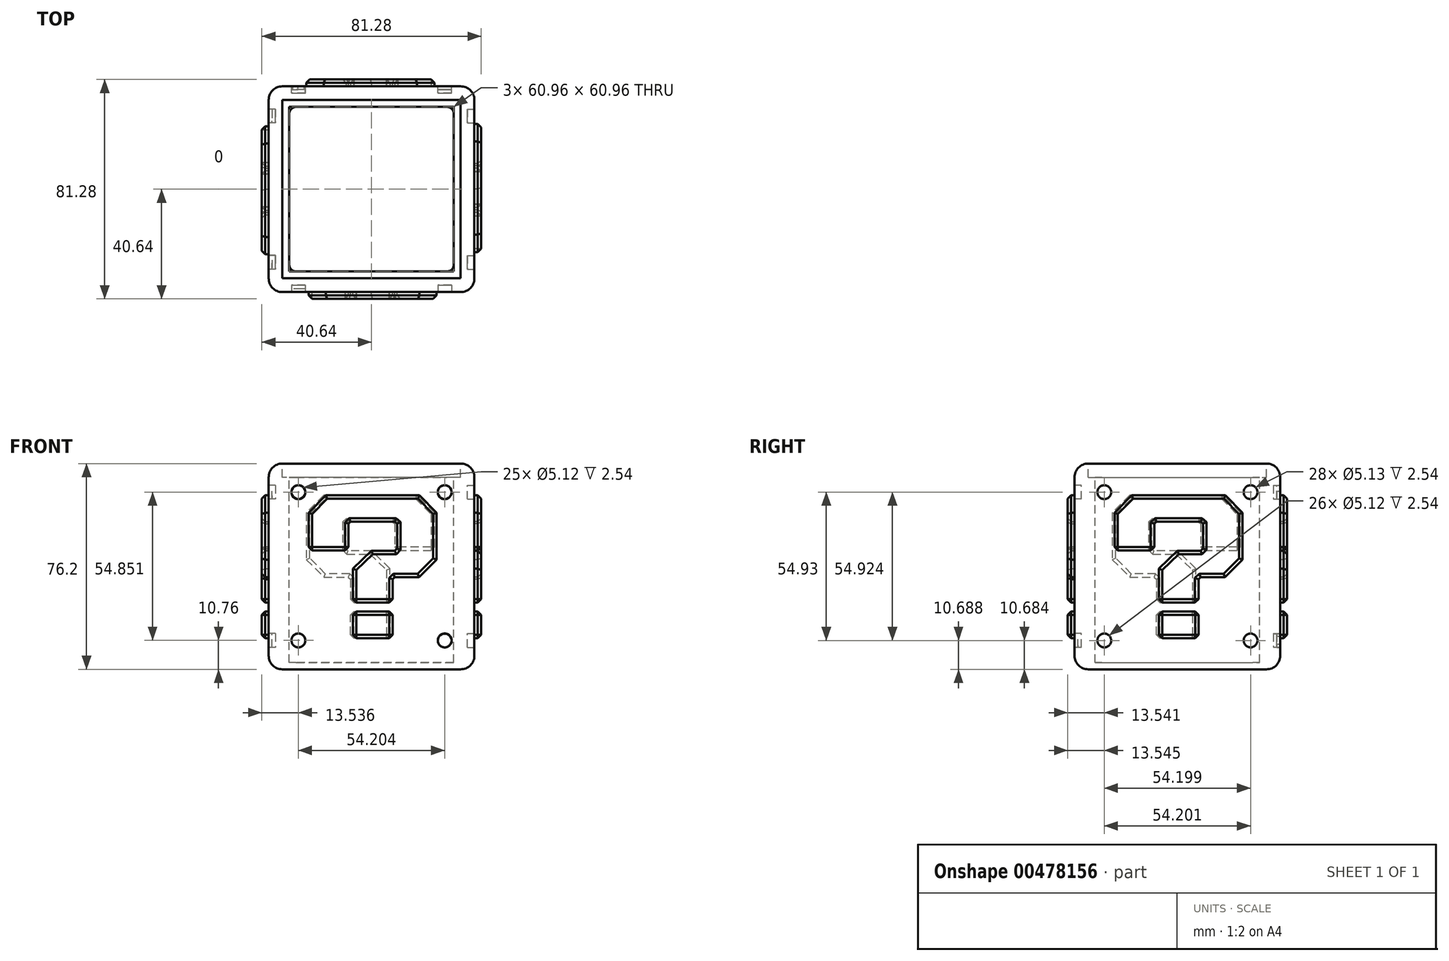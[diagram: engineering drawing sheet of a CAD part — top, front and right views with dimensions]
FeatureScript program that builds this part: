
annotation { "Feature Type Name" : "Feature", "Feature Type Description" : "" }
export const myFeature = defineFeature(function(context is Context, id is Id, definition is map)
    precondition{}
    {
        {
            var Q0;
            Q0=qCreatedBy(makeId("Top.planeOp"),FACE);
            var sketch = newSketch(context, id + "F0", { "sketchPlane" : qUnion([Q0])});
            skLineSegment(sketch, "E0.bottom", {"start": v(38.1, 38.1) * mm, "end": v(-38.1, 38.1) * mm});
            skLineSegment(sketch, "E0.top", {"start": v(38.1, -38.1) * mm, "end": v(-38.1, -38.1) * mm});
            skLineSegment(sketch, "E0.left", {"start": v(38.1, 38.1) * mm, "end": v(38.1, -38.1) * mm});
            skLineSegment(sketch, "E0.right", {"start": v(-38.1, 38.1) * mm, "end": v(-38.1, -38.1) * mm});
            skPoint(sketch, "E0.middle", {"position": v(0, 0) * mm});
            skSolve(sketch);
        }
        {
            var Q0;
            Q0=makeQuery(id+"F0.imprint","IMPRINT",FACE,{"disambiguationData":[TD([[makeQuery(id+"F0.imprint","IMPRINT",EDGE,{"derivedFrom":sQuery(id+"F0.wireOp",EDGE,"E0.bottom")}),1.0]])]});
            extrude(context, id + "F1", {"entities" : qUnion([Q0]), "depth" : 76.2 * mm, "offsetDistance" : 25.4 * mm});
        }
        {
            var Q0;
            Q0=makeQuery(id+"F1.opExtrude","CAP_FACE",FACE,{"disambiguationData":[OSD([sQuery(id+"F0.wireOp",EDGE,"E0.bottom"),sQuery(id+"F0.wireOp",EDGE,"E0.top"),sQuery(id+"F0.wireOp",EDGE,"E0.left"),sQuery(id+"F0.wireOp",EDGE,"E0.right")])],"isStart":true});
            var Q1;
            Q1=makeQuery(id+"F1.opExtrude","SWEPT_FACE",FACE,{"disambiguationData":[OSD([sQuery(id+"F0.wireOp",EDGE,"E0.bottom")])]});
            var Q2;
            Q2=makeQuery(id+"F1.opExtrude","SWEPT_FACE",FACE,{"disambiguationData":[OSD([sQuery(id+"F0.wireOp",EDGE,"E0.right")])]});
            var Q3;
            Q3=makeQuery(id+"F1.opExtrude","SWEPT_FACE",FACE,{"disambiguationData":[OSD([sQuery(id+"F0.wireOp",EDGE,"E0.left")])]});
            var Q4;
            Q4=makeQuery(id+"F1.opExtrude","SWEPT_FACE",FACE,{"disambiguationData":[OSD([sQuery(id+"F0.wireOp",EDGE,"E0.top")])]});
            var Q5;
            Q5=makeQuery(id+"F1.opExtrude","CAP_FACE",FACE,{"disambiguationData":[OSD([sQuery(id+"F0.wireOp",EDGE,"E0.bottom"),sQuery(id+"F0.wireOp",EDGE,"E0.top"),sQuery(id+"F0.wireOp",EDGE,"E0.left"),sQuery(id+"F0.wireOp",EDGE,"E0.right")])],"isStart":false});
            fillet(context, id + "F2", {"entities" : qUnion([Q0, Q1, Q2, Q3, Q4, Q5]), "radius" : 5.08 * mm, "tangentPropagation" : true, "allowEdgeOverflow" : false});
        }
        {
            var Q0;
            Q0=makeQuery(id+"F1.opExtrude","SWEPT_FACE",FACE,{"disambiguationData":[OSD([sQuery(id+"F0.wireOp",EDGE,"E0.left")])]});
            var sketch = newSketch(context, id + "F3", { "sketchPlane" : qUnion([Q0])});
            skLineSegment(sketch, "E1", {"start": v(0, 71.12) * mm, "end": v(0, 64.52) * mm});
            skPoint(sketch, "E1.endSnap0", {"position": v(0, 71.12) * mm});
            skLineSegment(sketch, "E2", {"start": v(0, 5.08) * mm, "end": v(0, 11.68) * mm});
            skPoint(sketch, "E2.endSnap0", {"position": v(0, 5.08) * mm});
            skSolve(sketch);
        }
        {
            var Q0;
            {var subQ0=sQuery(id+"F0.wireOp",EDGE,"E0.left");var subQ1=makeQuery(id+"F1.opExtrude","SWEPT_FACE",FACE,{"disambiguationData":[OSD([subQ0])]});var subQ5=makeQuery(id+"F2.opFillet","BLEND_EDGE",EDGE,{"blendedFrom":[makeQuery(id+"F1.opExtrude","SWEPT_EDGE",EDGE,{"disambiguationData":[OSD([sQuery(id+"F0.wireOp",EDGE,"E0.bottom"),subQ0])]}),subQ1],"blendedInto":[subQ1]});Q0=makeQuery(id+"F3.imprint","IMPRINT",FACE,{"disambiguationData":[TD([[makeQuery(id+"F3.imprint","IMPRINT",EDGE,{"derivedFrom":subQ5}),1.0]])]});}
            var sketch = newSketch(context, id + "F4", { "sketchPlane" : qUnion([Q0])});
            skLineSegment(sketch, "E3", {"start": v(-23.33, 57.98) * mm, "end": v(-16.9, 64.41) * mm});
            skLineSegment(sketch, "E4", {"start": v(-16.9, 64.41) * mm, "end": v(17.73, 64.41) * mm});
            skLineSegment(sketch, "E5", {"start": v(17.73, 64.41) * mm, "end": v(24.13, 58) * mm});
            skLineSegment(sketch, "E6", {"start": v(24.13, 58) * mm, "end": v(24.13, 40.64) * mm});
            skLineSegment(sketch, "E7", {"start": v(24.13, 40.64) * mm, "end": v(17.66, 34.17) * mm});
            skLineSegment(sketch, "E8", {"start": v(17.66, 34.17) * mm, "end": v(8.64, 34.17) * mm});
            skLineSegment(sketch, "E9", {"start": v(8.64, 34.17) * mm, "end": v(7.78, 33.32) * mm});
            skLineSegment(sketch, "E10", {"start": v(7.78, 33.32) * mm, "end": v(7.78, 24.73) * mm});
            skLineSegment(sketch, "E11", {"start": v(7.78, 24.73) * mm, "end": v(-6.86, 24.73) * mm});
            skLineSegment(sketch, "E12", {"start": v(-6.86, 24.73) * mm, "end": v(-6.86, 37.33) * mm});
            skLineSegment(sketch, "E13", {"start": v(-6.86, 37.33) * mm, "end": v(0, 43.94) * mm});
            skLineSegment(sketch, "E14", {"start": v(0, 43.94) * mm, "end": v(8.64, 43.94) * mm});
            skLineSegment(sketch, "E15", {"start": v(8.64, 43.94) * mm, "end": v(9.46, 44.76) * mm});
            skLineSegment(sketch, "E16", {"start": v(9.46, 44.76) * mm, "end": v(9.46, 53.96) * mm});
            skLineSegment(sketch, "E17", {"start": v(9.46, 53.96) * mm, "end": v(8.64, 54.74) * mm});
            skLineSegment(sketch, "E18", {"start": v(8.64, 54.74) * mm, "end": v(-7.76, 54.74) * mm});
            skLineSegment(sketch, "E19", {"start": v(-7.76, 54.74) * mm, "end": v(-8.6, 53.9) * mm});
            skLineSegment(sketch, "E20", {"start": v(-8.6, 53.9) * mm, "end": v(-8.6, 44.03) * mm});
            skLineSegment(sketch, "E21", {"start": v(-8.6, 44.03) * mm, "end": v(-23.33, 44.03) * mm});
            skLineSegment(sketch, "E22", {"start": v(-23.33, 44.03) * mm, "end": v(-23.33, 57.98) * mm});
            skLineSegment(sketch, "E23", {"start": v(-6.85, 21.4) * mm, "end": v(-6.85, 11.58) * mm});
            skLineSegment(sketch, "E24", {"start": v(-6.85, 11.58) * mm, "end": v(7.8, 11.58) * mm});
            skLineSegment(sketch, "E25", {"start": v(7.8, 11.58) * mm, "end": v(7.8, 21.4) * mm});
            skLineSegment(sketch, "E26", {"start": v(7.8, 21.4) * mm, "end": v(-6.85, 21.4) * mm});
            skPoint(sketch, "E27.start.orphan", {"position": v(-23.33, 51) * mm});
            skSolve(sketch);
        }
        {
            var Q0;
            {var subQ0=sQuery(id+"F0.wireOp",EDGE,"E0.left");var subQ1=makeQuery(id+"F1.opExtrude","SWEPT_FACE",FACE,{"disambiguationData":[OSD([subQ0])]});var subQ5=makeQuery(id+"F2.opFillet","BLEND_EDGE",EDGE,{"blendedFrom":[makeQuery(id+"F1.opExtrude","SWEPT_EDGE",EDGE,{"disambiguationData":[OSD([sQuery(id+"F0.wireOp",EDGE,"E0.bottom"),subQ0])]}),subQ1],"blendedInto":[subQ1]});Q0=makeQuery(id+"F3.imprint","IMPRINT",FACE,{"disambiguationData":[TD([[makeQuery(id+"F3.imprint","IMPRINT",EDGE,{"derivedFrom":subQ5}),1.0]])]});}
            var sketch = newSketch(context, id + "F5", { "sketchPlane" : qUnion([Q0])});
            skCircle(sketch, "E28", {"center": v(-27.1, 10.68) * mm, "radius": 2.56 * mm});
            skPoint(sketch, "E28.first.point", {"position": v(-29.65, 10.95) * mm});
            skPoint(sketch, "E28.second.point", {"position": v(-24.55, 10.4) * mm});
            skPoint(sketch, "E28.third.point", {"position": v(-26.75, 8.14) * mm});
            skCircle(sketch, "E29.MirrorC", {"center": v(-27.1, 65.6) * mm, "radius": 2.56 * mm});
            skCircle(sketch, "E30.MirrorC", {"center": v(27.1, 65.6) * mm, "radius": 2.56 * mm});
            skCircle(sketch, "E31.MirrorC", {"center": v(27.1, 10.68) * mm, "radius": 2.56 * mm});
            skSolve(sketch);
        }
        {
            var Q0;
            Q0 = qSketchRegion(id + "F4", true);
            extrude(context, id + "F6", {"entities" : qUnion([Q0]), "operationType" : NewBodyOperationType.ADD, "depth" : 2.54 * mm, "offsetDistance" : 25.4 * mm});
        }
        {
            var Q0;
            Q0=makeQuery(id+"F6.opExtrude","CAP_EDGE",EDGE,{"disambiguationData":[OSD([sQuery(id+"F4.wireOp",EDGE,"E4")])],"isStart":false});
            var Q1;
            Q1=makeQuery(id+"F6.opExtrude","CAP_EDGE",EDGE,{"disambiguationData":[OSD([sQuery(id+"F4.wireOp",EDGE,"E3")])],"isStart":false});
            var Q2;
            Q2=makeQuery(id+"F6.opExtrude","CAP_EDGE",EDGE,{"disambiguationData":[OSD([sQuery(id+"F4.wireOp",EDGE,"E22")])],"isStart":false});
            var Q3;
            Q3=makeQuery(id+"F6.opExtrude","CAP_EDGE",EDGE,{"disambiguationData":[OSD([sQuery(id+"F4.wireOp",EDGE,"E21")])],"isStart":false});
            var Q4;
            Q4=makeQuery(id+"F6.opExtrude","CAP_EDGE",EDGE,{"disambiguationData":[OSD([sQuery(id+"F4.wireOp",EDGE,"E20")])],"isStart":false});
            var Q5;
            Q5=makeQuery(id+"F6.opExtrude","CAP_EDGE",EDGE,{"disambiguationData":[OSD([sQuery(id+"F4.wireOp",EDGE,"E19")])],"isStart":false});
            var Q6;
            Q6=makeQuery(id+"F6.opExtrude","CAP_EDGE",EDGE,{"disambiguationData":[OSD([sQuery(id+"F4.wireOp",EDGE,"E18")])],"isStart":false});
            var Q7;
            Q7=makeQuery(id+"F6.opExtrude","CAP_FACE",FACE,{"disambiguationData":[OSD([sQuery(id+"F4.wireOp",EDGE,"E3"),sQuery(id+"F4.wireOp",EDGE,"E4"),sQuery(id+"F4.wireOp",EDGE,"E5"),sQuery(id+"F4.wireOp",EDGE,"E6"),sQuery(id+"F4.wireOp",EDGE,"E7"),sQuery(id+"F4.wireOp",EDGE,"E8"),sQuery(id+"F4.wireOp",EDGE,"E9"),sQuery(id+"F4.wireOp",EDGE,"E10"),sQuery(id+"F4.wireOp",EDGE,"E11"),sQuery(id+"F4.wireOp",EDGE,"E12"),sQuery(id+"F4.wireOp",EDGE,"E13"),sQuery(id+"F4.wireOp",EDGE,"E14"),sQuery(id+"F4.wireOp",EDGE,"E15"),sQuery(id+"F4.wireOp",EDGE,"E16"),sQuery(id+"F4.wireOp",EDGE,"E17"),sQuery(id+"F4.wireOp",EDGE,"E18"),sQuery(id+"F4.wireOp",EDGE,"E19"),sQuery(id+"F4.wireOp",EDGE,"E20"),sQuery(id+"F4.wireOp",EDGE,"E21"),sQuery(id+"F4.wireOp",EDGE,"E22")])],"isStart":false});
            var Q8;
            Q8=makeQuery(id+"F6.opExtrude","CAP_FACE",FACE,{"disambiguationData":[OSD([sQuery(id+"F4.wireOp",EDGE,"E23"),sQuery(id+"F4.wireOp",EDGE,"E24"),sQuery(id+"F4.wireOp",EDGE,"E25"),sQuery(id+"F4.wireOp",EDGE,"E26")])],"isStart":false});
            var Q9;
            Q9=makeQuery(id+"F6.opExtrude","SWEPT_EDGE",EDGE,{"disambiguationData":[OSD([sQuery(id+"F4.wireOp",EDGE,"E23"),sQuery(id+"F4.wireOp",EDGE,"E24")])]});
            var Q10;
            Q10=makeQuery(id+"F6.opExtrude","SWEPT_EDGE",EDGE,{"disambiguationData":[OSD([sQuery(id+"F4.wireOp",EDGE,"E21"),sQuery(id+"F4.wireOp",EDGE,"E22")])]});
            var Q11;
            Q11=makeQuery(id+"F6.opExtrude","SWEPT_EDGE",EDGE,{"disambiguationData":[OSD([sQuery(id+"F4.wireOp",EDGE,"E20"),sQuery(id+"F4.wireOp",EDGE,"E21")])]});
            var Q12;
            Q12=makeQuery(id+"F6.opExtrude","SWEPT_EDGE",EDGE,{"disambiguationData":[OSD([sQuery(id+"F4.wireOp",EDGE,"E10"),sQuery(id+"F4.wireOp",EDGE,"E11")])]});
            var Q13;
            Q13=makeQuery(id+"F6.opExtrude","SWEPT_EDGE",EDGE,{"disambiguationData":[OSD([sQuery(id+"F4.wireOp",EDGE,"E11"),sQuery(id+"F4.wireOp",EDGE,"E12")])]});
            var Q14;
            Q14=makeQuery(id+"F6.opExtrude","SWEPT_EDGE",EDGE,{"disambiguationData":[OSD([sQuery(id+"F4.wireOp",EDGE,"E25"),sQuery(id+"F4.wireOp",EDGE,"E26")])]});
            var Q15;
            Q15=makeQuery(id+"F6.opExtrude","SWEPT_EDGE",EDGE,{"disambiguationData":[OSD([sQuery(id+"F4.wireOp",EDGE,"E24"),sQuery(id+"F4.wireOp",EDGE,"E25")])]});
            var Q16;
            Q16=makeQuery(id+"F6.opExtrude","SWEPT_EDGE",EDGE,{"disambiguationData":[OSD([sQuery(id+"F4.wireOp",EDGE,"E23"),sQuery(id+"F4.wireOp",EDGE,"E26")])]});
            chamfer(context, id + "F7", {"entities" : qUnion([Q0, Q1, Q2, Q3, Q4, Q5, Q6, Q7, Q8, Q9, Q10, Q11, Q12, Q13, Q14, Q15, Q16]), "width" : 1.27 * mm, "tangentPropagation" : true});
        }
        {
            var Q0;
            Q0=qCreatedBy(makeId("Right.planeOp"),FACE);
            var sketch = newSketch(context, id + "F8", { "sketchPlane" : qUnion([Q0])});
            skLineSegment(sketch, "E32", {"start": v(0, 0) * mm, "end": v(0, 88.63) * mm});
            skSolve(sketch);
        }
        {
            var Q0;
            Q0=makeQuery(id+"F1.opExtrude","SWEPT_BODY",BODY,{"disambiguationData":[OSD([sQuery(id+"F0.wireOp",EDGE,"E0.bottom"),sQuery(id+"F0.wireOp",EDGE,"E0.top"),sQuery(id+"F0.wireOp",EDGE,"E0.left"),sQuery(id+"F0.wireOp",EDGE,"E0.right")])]});
            var Q1;
            Q1=sQuery(id+"F8.wireOp",EDGE,"E32");
            transform(context, id + "F9", {"entities" : qUnion([Q0]), "transformType" : TransformType.ROTATION, "transformAxis" : qUnion([Q1]), "angle" : 90 * degree, "makeCopy" : true});
        }
        {
            var Q0;
            Q0=qCreatedBy(makeId("Front.planeOp"),FACE);
            var sketch = newSketch(context, id + "F10", { "sketchPlane" : qUnion([Q0])});
            skLineSegment(sketch, "E33", {"start": v(0, 0) * mm, "end": v(0, 84.32) * mm});
            skSolve(sketch);
        }
        {
            var Q0;
            Q0=makeQuery(id+"F1.opExtrude","SWEPT_BODY",BODY,{"disambiguationData":[OSD([sQuery(id+"F0.wireOp",EDGE,"E0.bottom"),sQuery(id+"F0.wireOp",EDGE,"E0.top"),sQuery(id+"F0.wireOp",EDGE,"E0.left"),sQuery(id+"F0.wireOp",EDGE,"E0.right")])]});
            var Q1;
            Q1=sQuery(id+"F10.wireOp",EDGE,"E33");
            transform(context, id + "F11", {"entities" : qUnion([Q0]), "transformType" : TransformType.ROTATION, "transformAxis" : qUnion([Q1]), "angle" : 180 * degree, "makeCopy" : true});
        }
        {
            var Q0;
            Q0=qCreatedBy(makeId("Right.planeOp"),FACE);
            var sketch = newSketch(context, id + "F12", { "sketchPlane" : qUnion([Q0])});
            skLineSegment(sketch, "E34", {"start": v(0, 0) * mm, "end": v(0, 95.89) * mm});
            skSolve(sketch);
        }
        {
            var Q0;
            Q0=makeQuery(id+"F11.opPattern","COPY",BODY,{"derivedFrom":makeQuery(id+"F1.opExtrude","SWEPT_BODY",BODY,{"disambiguationData":[OSD([sQuery(id+"F0.wireOp",EDGE,"E0.bottom"),sQuery(id+"F0.wireOp",EDGE,"E0.top"),sQuery(id+"F0.wireOp",EDGE,"E0.left"),sQuery(id+"F0.wireOp",EDGE,"E0.right")])]}),"instanceName":"1"});
            var Q1;
            Q1=sQuery(id+"F12.wireOp",EDGE,"E34");
            transform(context, id + "F13", {"entities" : qUnion([Q0]), "transformType" : TransformType.ROTATION, "transformAxis" : qUnion([Q1]), "angle" : 90 * degree, "makeCopy" : true});
        }
        {
            var Q0;
            Q0=makeQuery(id+"F1.opExtrude","CAP_FACE",FACE,{"disambiguationData":[OSD([sQuery(id+"F0.wireOp",EDGE,"E0.bottom"),sQuery(id+"F0.wireOp",EDGE,"E0.top"),sQuery(id+"F0.wireOp",EDGE,"E0.left"),sQuery(id+"F0.wireOp",EDGE,"E0.right")])],"isStart":false});
            extrude(context, id + "F14", {"entities" : qUnion([Q0]), "operationType" : NewBodyOperationType.REMOVE, "oppositeDirection" : true, "depth" : 5.08 * mm, "offsetDistance" : 25.4 * mm});
        }
        {
            var Q0;
            Q0=makeQuery(id+"F14.boolean.opBoolean","COPY",FACE,{"disambiguationData":[OD(1.0)],"derivedFrom":makeQuery(id+"F14.opExtrude","CAP_FACE",FACE,{"disambiguationData":[OSD([sQuery(id+"F0.wireOp",EDGE,"E0.bottom"),sQuery(id+"F0.wireOp",EDGE,"E0.top"),sQuery(id+"F0.wireOp",EDGE,"E0.left"),sQuery(id+"F0.wireOp",EDGE,"E0.right")])],"isStart":false})});
            var sketch = newSketch(context, id + "F15", { "sketchPlane" : qUnion([Q0])});
            skLineSegment(sketch, "E35.bottom", {"start": v(30.48, 30.48) * mm, "end": v(-30.48, 30.48) * mm});
            skLineSegment(sketch, "E35.top", {"start": v(30.48, -30.48) * mm, "end": v(-30.48, -30.48) * mm});
            skLineSegment(sketch, "E35.left", {"start": v(30.48, 30.48) * mm, "end": v(30.48, -30.48) * mm});
            skLineSegment(sketch, "E35.right", {"start": v(-30.48, 30.48) * mm, "end": v(-30.48, -30.48) * mm});
            skPoint(sketch, "E35.middle", {"position": v(0, 0) * mm});
            skSolve(sketch);
        }
        {
            var Q0;
            Q0=makeQuery(id+"F15.imprint","IMPRINT",FACE,{"disambiguationData":[TD([[makeQuery(id+"F15.imprint","IMPRINT",EDGE,{"derivedFrom":sQuery(id+"F15.wireOp",EDGE,"E35.bottom")}),1.0]])]});
            extrude(context, id + "F16", {"entities" : qUnion([Q0]), "operationType" : NewBodyOperationType.REMOVE, "oppositeDirection" : true, "depth" : 68.58 * mm, "offsetDistance" : 25.4 * mm});
        }
        {
            var Q0;
            {var subQ0=sQuery(id+"F15.wireOp",EDGE,"E35.right");var subQ1=sQuery(id+"F15.wireOp",EDGE,"E35.top");Q0=makeQuery(id+"F16.boolean.opBoolean","COPY",EDGE,{"disambiguationData":[TD([makeQuery(id+"F14.boolean.opBoolean","COPY",FACE,{"disambiguationData":[OD(1.0)],"derivedFrom":makeQuery(id+"F14.opExtrude","CAP_FACE",FACE,{"disambiguationData":[OSD([sQuery(id+"F0.wireOp",EDGE,"E0.bottom"),sQuery(id+"F0.wireOp",EDGE,"E0.top"),sQuery(id+"F0.wireOp",EDGE,"E0.left"),sQuery(id+"F0.wireOp",EDGE,"E0.right")])],"isStart":false})})])],"derivedFrom":makeQuery(id+"F16.opExtrude","SWEPT_EDGE",EDGE,{"disambiguationData":[OSD([subQ1,subQ0])]})});}
            var Q1;
            {var subQ0=sQuery(id+"F15.wireOp",EDGE,"E35.bottom");var subQ1=sQuery(id+"F15.wireOp",EDGE,"E35.right");Q1=makeQuery(id+"F16.boolean.opBoolean","COPY",EDGE,{"disambiguationData":[TD([makeQuery(id+"F14.boolean.opBoolean","COPY",FACE,{"disambiguationData":[OD(1.0)],"derivedFrom":makeQuery(id+"F14.opExtrude","CAP_FACE",FACE,{"disambiguationData":[OSD([sQuery(id+"F0.wireOp",EDGE,"E0.bottom"),sQuery(id+"F0.wireOp",EDGE,"E0.top"),sQuery(id+"F0.wireOp",EDGE,"E0.left"),sQuery(id+"F0.wireOp",EDGE,"E0.right")])],"isStart":false})})])],"derivedFrom":makeQuery(id+"F16.opExtrude","SWEPT_EDGE",EDGE,{"disambiguationData":[OSD([subQ0,subQ1])]})});}
            var Q2;
            {var subQ0=sQuery(id+"F15.wireOp",EDGE,"E35.left");var subQ1=sQuery(id+"F15.wireOp",EDGE,"E35.bottom");Q2=makeQuery(id+"F16.boolean.opBoolean","COPY",EDGE,{"disambiguationData":[TD([makeQuery(id+"F14.boolean.opBoolean","COPY",FACE,{"disambiguationData":[OD(1.0)],"derivedFrom":makeQuery(id+"F14.opExtrude","CAP_FACE",FACE,{"disambiguationData":[OSD([sQuery(id+"F0.wireOp",EDGE,"E0.bottom"),sQuery(id+"F0.wireOp",EDGE,"E0.top"),sQuery(id+"F0.wireOp",EDGE,"E0.left"),sQuery(id+"F0.wireOp",EDGE,"E0.right")])],"isStart":false})})])],"derivedFrom":makeQuery(id+"F16.opExtrude","SWEPT_EDGE",EDGE,{"disambiguationData":[OSD([subQ1,subQ0])]})});}
            var Q3;
            {var subQ0=sQuery(id+"F15.wireOp",EDGE,"E35.left");var subQ1=sQuery(id+"F15.wireOp",EDGE,"E35.top");Q3=makeQuery(id+"F16.boolean.opBoolean","COPY",EDGE,{"disambiguationData":[TD([makeQuery(id+"F14.boolean.opBoolean","COPY",FACE,{"disambiguationData":[OD(1.0)],"derivedFrom":makeQuery(id+"F14.opExtrude","CAP_FACE",FACE,{"disambiguationData":[OSD([sQuery(id+"F0.wireOp",EDGE,"E0.bottom"),sQuery(id+"F0.wireOp",EDGE,"E0.top"),sQuery(id+"F0.wireOp",EDGE,"E0.left"),sQuery(id+"F0.wireOp",EDGE,"E0.right")])],"isStart":false})})])],"derivedFrom":makeQuery(id+"F16.opExtrude","SWEPT_EDGE",EDGE,{"disambiguationData":[OSD([subQ1,subQ0])]})});}
            fillet(context, id + "F17", {"entities" : qUnion([Q0, Q1, Q2, Q3]), "radius" : 2.54 * mm, "tangentPropagation" : true, "allowEdgeOverflow" : false});
        }
        {
            var Q0;
            Q0 = qSketchRegion(id + "F5", true);
            extrude(context, id + "F18", {"entities" : qUnion([Q0]), "operationType" : NewBodyOperationType.REMOVE, "oppositeDirection" : true, "depth" : 1.27 * mm, "offsetDistance" : 25.4 * mm});
        }
        {
            var Q0;
            Q0=qCreatedBy(makeId("Front.planeOp"),FACE);
            var sketch = newSketch(context, id + "F19", { "sketchPlane" : qUnion([Q0])});
            skLineSegment(sketch, "E36", {"start": v(0, 0) * mm, "end": v(0, 92.85) * mm});
            skSolve(sketch);
        }
        {
            var Q0;
            Q0=makeQuery(id+"F1.opExtrude","SWEPT_BODY",BODY,{"disambiguationData":[OSD([sQuery(id+"F0.wireOp",EDGE,"E0.bottom"),sQuery(id+"F0.wireOp",EDGE,"E0.top"),sQuery(id+"F0.wireOp",EDGE,"E0.left"),sQuery(id+"F0.wireOp",EDGE,"E0.right")])]});
            var Q1;
            Q1=sQuery(id+"F19.wireOp",EDGE,"E36");
            transform(context, id + "F20", {"entities" : qUnion([Q0]), "transformType" : TransformType.ROTATION, "transformAxis" : qUnion([Q1]), "angle" : 90 * degree, "makeCopy" : true});
        }
        {
            var Q0;
            Q0=qCreatedBy(makeId("Front.planeOp"),FACE);
            var sketch = newSketch(context, id + "F21", { "sketchPlane" : qUnion([Q0])});
            skLineSegment(sketch, "E37", {"start": v(0, 0) * mm, "end": v(0, 95.22) * mm});
            skSolve(sketch);
        }
        {
            var Q0;
            Q0=makeQuery(id+"F9.opPattern","COPY",BODY,{"derivedFrom":makeQuery(id+"F1.opExtrude","SWEPT_BODY",BODY,{"disambiguationData":[OSD([sQuery(id+"F0.wireOp",EDGE,"E0.bottom"),sQuery(id+"F0.wireOp",EDGE,"E0.top"),sQuery(id+"F0.wireOp",EDGE,"E0.left"),sQuery(id+"F0.wireOp",EDGE,"E0.right")])]}),"instanceName":"1"});
            var Q1;
            Q1=sQuery(id+"F21.wireOp",EDGE,"E37");
            transform(context, id + "F22", {"entities" : qUnion([Q0]), "transformType" : TransformType.ROTATION, "transformAxis" : qUnion([Q1]), "angle" : 180 * degree, "makeCopy" : true});
        }
        {
            var Q0;
            Q0=qCreatedBy(makeId("Right.planeOp"),FACE);
            var sketch = newSketch(context, id + "F23", { "sketchPlane" : qUnion([Q0])});
            skLineSegment(sketch, "E38", {"start": v(0, 0) * mm, "end": v(0, 110.55) * mm});
            skSolve(sketch);
        }
        {
            var Q0;
            Q0=makeQuery(id+"F11.opPattern","COPY",BODY,{"derivedFrom":makeQuery(id+"F1.opExtrude","SWEPT_BODY",BODY,{"disambiguationData":[OSD([sQuery(id+"F0.wireOp",EDGE,"E0.bottom"),sQuery(id+"F0.wireOp",EDGE,"E0.top"),sQuery(id+"F0.wireOp",EDGE,"E0.left"),sQuery(id+"F0.wireOp",EDGE,"E0.right")])]}),"instanceName":"1"});
            var Q1;
            Q1=sQuery(id+"F23.wireOp",EDGE,"E38");
            transform(context, id + "F24", {"entities" : qUnion([Q0]), "transformType" : TransformType.ROTATION, "transformAxis" : qUnion([Q1]), "angle" : 270 * degree, "makeCopy" : true});
        }
        {
            var Q0;
            Q0 = qSketchRegion(id + "F5", true);
            var Q1;
            Q1 = qSketchRegion(id + "F19", true);
            extrude(context, id + "F25", {"entities" : qUnion([Q0, Q1]), "operationType" : NewBodyOperationType.REMOVE, "oppositeDirection" : true, "depth" : 2.54 * mm, "offsetDistance" : 25.4 * mm});
        }
        {
            var Q0;
            Q0=makeQuery(id+"F1.opExtrude","SWEPT_FACE",FACE,{"disambiguationData":[OSD([sQuery(id+"F0.wireOp",EDGE,"E0.bottom")])]});
            var sketch = newSketch(context, id + "F26", { "sketchPlane" : qUnion([Q0])});
            skCircle(sketch, "E39", {"center": v(-27.1, 65.6) * mm, "radius": 2.56 * mm});
            skPoint(sketch, "E39.first.point", {"position": v(-25.48, 63.63) * mm});
            skPoint(sketch, "E39.second.point", {"position": v(-29.5, 66.5) * mm});
            skPoint(sketch, "E39.third.point", {"position": v(-28.77, 63.67) * mm});
            skSolve(sketch);
        }
        {
            var Q0;
            Q0=makeQuery(id+"F26.imprint","IMPRINT",FACE,{"disambiguationData":[TD([[makeQuery(id+"F26.imprint","IMPRINT",EDGE,{"derivedFrom":sQuery(id+"F26.wireOp",EDGE,"E39")}),-1.0]])]});
            var sketch = newSketch(context, id + "F27", { "sketchPlane" : qUnion([Q0])});
            skCircle(sketch, "E40", {"center": v(-27.1, 10.67) * mm, "radius": 2.52 * mm});
            skPoint(sketch, "E40.first.point", {"position": v(-27, 13.19) * mm});
            skPoint(sketch, "E40.second.point", {"position": v(-25.09, 9.16) * mm});
            skPoint(sketch, "E40.third.point", {"position": v(-29.44, 9.76) * mm});
            skCircle(sketch, "E41", {"center": v(27.05, 10.76) * mm, "radius": 2.56 * mm});
            skPoint(sketch, "E41.first.point", {"position": v(26.99, 13.32) * mm});
            skPoint(sketch, "E41.second.point", {"position": v(29.43, 9.82) * mm});
            skPoint(sketch, "E41.third.point", {"position": v(26.33, 8.3) * mm});
            skCircle(sketch, "E42", {"center": v(27.06, 65.65) * mm, "radius": 2.52 * mm});
            skPoint(sketch, "E42.first.point", {"position": v(27.9, 63.28) * mm});
            skPoint(sketch, "E42.second.point", {"position": v(28.44, 67.77) * mm});
            skPoint(sketch, "E42.third.point", {"position": v(24.54, 65.59) * mm});
            skSolve(sketch);
        }
        {
            var Q0;
            Q0=makeQuery(id+"F26.imprint","IMPRINT",FACE,{"disambiguationData":[TD([[makeQuery(id+"F26.imprint","IMPRINT",EDGE,{"derivedFrom":sQuery(id+"F26.wireOp",EDGE,"E39")}),1.0]])]});
            extrude(context, id + "F28", {"entities" : qUnion([Q0]), "operationType" : NewBodyOperationType.REMOVE, "oppositeDirection" : true, "depth" : 2.54 * mm, "offsetDistance" : 25.4 * mm});
        }
        {
            var Q0;
            Q0 = qSketchRegion(id + "F27", true);
            extrude(context, id + "F29", {"entities" : qUnion([Q0]), "operationType" : NewBodyOperationType.REMOVE, "oppositeDirection" : true, "depth" : 2.54 * mm, "offsetDistance" : 25.4 * mm});
        }
        {
            var Q0;
            Q0=makeQuery(id+"F1.opExtrude","SWEPT_FACE",FACE,{"disambiguationData":[OSD([sQuery(id+"F0.wireOp",EDGE,"E0.right")])]});
            var sketch = newSketch(context, id + "F30", { "sketchPlane" : qUnion([Q0])});
            skSolve(sketch);
        }
        {
            var Q0;
            {var subQ0=sQuery(id+"F0.wireOp",EDGE,"E0.right");var subQ1=makeQuery(id+"F1.opExtrude","SWEPT_FACE",FACE,{"disambiguationData":[OSD([subQ0])]});Q0=makeQuery(id+"F30.imprint","IMPRINT",FACE,{"disambiguationData":[TD([[makeQuery(id+"F30.imprint","IMPRINT",EDGE,{"derivedFrom":makeQuery(id+"F2.opFillet","BLEND_EDGE",EDGE,{"blendedFrom":[makeQuery(id+"F1.opExtrude","CAP_EDGE",EDGE,{"disambiguationData":[OSD([subQ0])],"isStart":true}),subQ1],"blendedInto":[subQ1]})}),1.0]])]});}
            var sketch = newSketch(context, id + "F31", { "sketchPlane" : qUnion([Q0])});
            skCircle(sketch, "E43", {"center": v(-27.1, 65.62) * mm, "radius": 2.56 * mm});
            skPoint(sketch, "E43.first.point", {"position": v(-26.05, 67.95) * mm});
            skPoint(sketch, "E43.second.point", {"position": v(-25.34, 63.76) * mm});
            skPoint(sketch, "E43.third.point", {"position": v(-29.63, 65.17) * mm});
            skCircle(sketch, "E44", {"center": v(27.1, 65.6) * mm, "radius": 2.56 * mm});
            skPoint(sketch, "E44.first.point", {"position": v(27.43, 68.15) * mm});
            skPoint(sketch, "E44.second.point", {"position": v(29.28, 64.28) * mm});
            skPoint(sketch, "E44.third.point", {"position": v(25.2, 63.88) * mm});
            skCircle(sketch, "E45", {"center": v(27.08, 10.69) * mm, "radius": 2.56 * mm});
            skPoint(sketch, "E45.first.point", {"position": v(28.4, 12.89) * mm});
            skPoint(sketch, "E45.second.point", {"position": v(28.62, 8.64) * mm});
            skPoint(sketch, "E45.third.point", {"position": v(24.69, 9.79) * mm});
            skCircle(sketch, "E46", {"center": v(-27.1, 10.69) * mm, "radius": 2.56 * mm});
            skPoint(sketch, "E46.first.point", {"position": v(-26.55, 13.19) * mm});
            skPoint(sketch, "E46.second.point", {"position": v(-25.06, 9.14) * mm});
            skPoint(sketch, "E46.third.point", {"position": v(-28.33, 8.44) * mm});
            skSolve(sketch);
        }
        {
            var Q0;
            Q0 = qSketchRegion(id + "F31", true);
            extrude(context, id + "F32", {"entities" : qUnion([Q0]), "operationType" : NewBodyOperationType.REMOVE, "oppositeDirection" : true, "depth" : 2.54 * mm, "offsetDistance" : 25.4 * mm});
        }
        {
            var Q0;
            Q0=makeQuery(id+"F1.opExtrude","SWEPT_FACE",FACE,{"disambiguationData":[OSD([sQuery(id+"F0.wireOp",EDGE,"E0.top")])]});
            var sketch = newSketch(context, id + "F33", { "sketchPlane" : qUnion([Q0])});
            skCircle(sketch, "E47", {"center": v(-27.1, 65.61) * mm, "radius": 2.56 * mm});
            skPoint(sketch, "E47.first.point", {"position": v(-28.5, 67.76) * mm});
            skPoint(sketch, "E47.second.point", {"position": v(-24.58, 66.06) * mm});
            skPoint(sketch, "E47.third.point", {"position": v(-27.7, 63.12) * mm});
            skCircle(sketch, "E48", {"center": v(27.1, 65.61) * mm, "radius": 2.56 * mm});
            skPoint(sketch, "E48.first.point", {"position": v(27.42, 68.15) * mm});
            skPoint(sketch, "E48.second.point", {"position": v(29.48, 64.68) * mm});
            skPoint(sketch, "E48.third.point", {"position": v(25.87, 63.37) * mm});
            skCircle(sketch, "E49", {"center": v(27.1, 10.69) * mm, "radius": 2.56 * mm});
            skPoint(sketch, "E49.first.point", {"position": v(27.23, 13.25) * mm});
            skPoint(sketch, "E49.second.point", {"position": v(29.25, 9.3) * mm});
            skPoint(sketch, "E49.third.point", {"position": v(26.37, 8.23) * mm});
            skCircle(sketch, "E50", {"center": v(-27.11, 10.7) * mm, "radius": 2.57 * mm});
            skPoint(sketch, "E50.first.point", {"position": v(-24.6, 11.2) * mm});
            skPoint(sketch, "E50.second.point", {"position": v(-28.7, 8.68) * mm});
            skPoint(sketch, "E50.third.point", {"position": v(-25.5, 8.7) * mm});
            skSolve(sketch);
        }
        {
            var Q0;
            Q0 = qSketchRegion(id + "F33", true);
            extrude(context, id + "F34", {"entities" : qUnion([Q0]), "operationType" : NewBodyOperationType.REMOVE, "oppositeDirection" : true, "depth" : 2.54 * mm, "offsetDistance" : 25.4 * mm});
        }
    });
